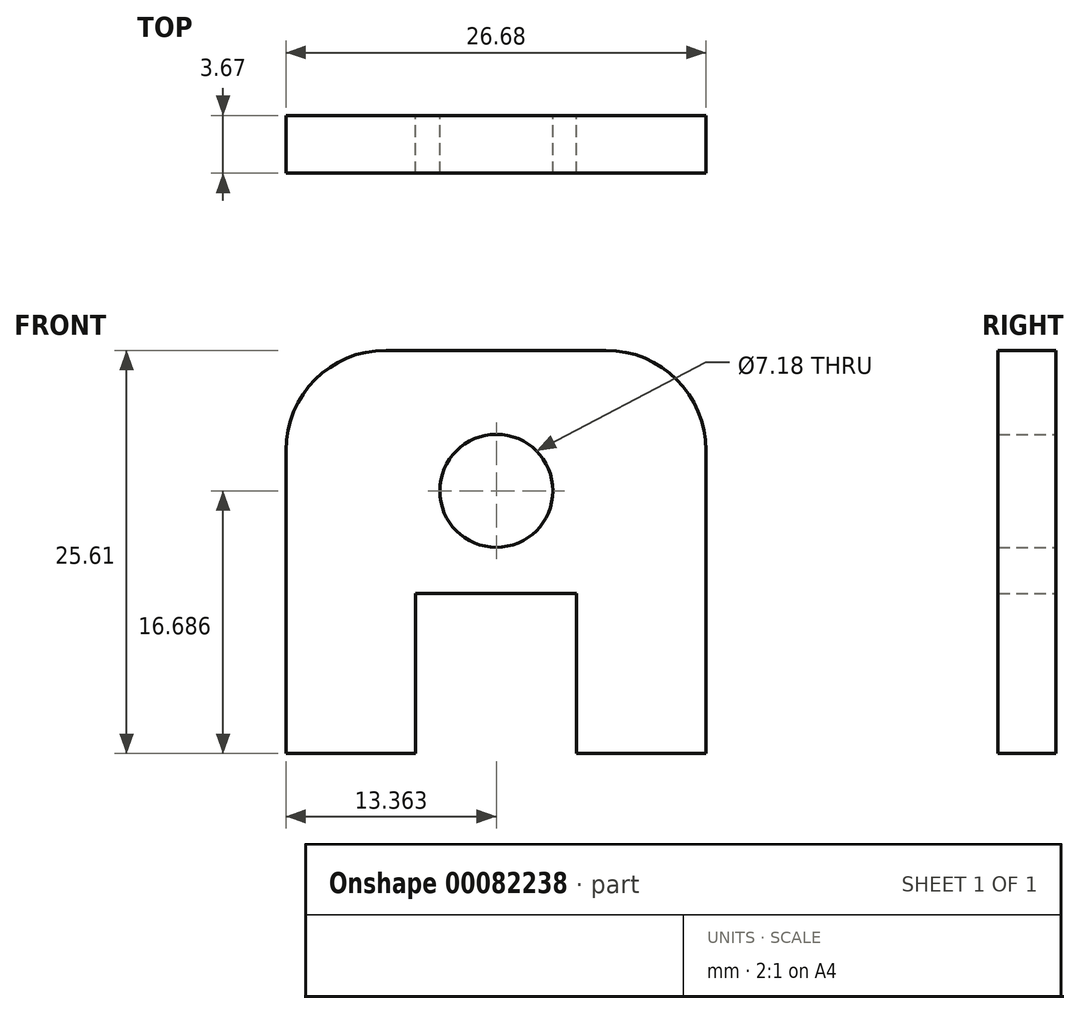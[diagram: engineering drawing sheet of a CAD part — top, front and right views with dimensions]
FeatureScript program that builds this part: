
annotation { "Feature Type Name" : "Feature", "Feature Type Description" : "" }
export const myFeature = defineFeature(function(context is Context, id is Id, definition is map)
    precondition{}
    {
        {
            var Q0;
            Q0=qCreatedBy(makeId("Front.planeOp"),FACE);
            var sketch = newSketch(context, id + "F0", { "sketchPlane" : qUnion([Q0])});
            skLineSegment(sketch, "E0", {"start": v(-46.74, 10.16) * mm, "end": v(-46.74, 0) * mm});
            skLineSegment(sketch, "E1", {"start": v(-46.74, 0) * mm, "end": v(-38.52, 0) * mm});
            skLineSegment(sketch, "E2", {"start": v(-38.52, 0) * mm, "end": v(-38.52, 10.16) * mm});
            skLineSegment(sketch, "E3", {"start": v(-38.52, 10.16) * mm, "end": v(-28.28, 10.16) * mm});
            skLineSegment(sketch, "E4", {"start": v(-28.28, 10.16) * mm, "end": v(-28.28, 0) * mm});
            skLineSegment(sketch, "E5", {"start": v(-28.28, 0) * mm, "end": v(-20.06, 0) * mm});
            skLineSegment(sketch, "E6", {"start": v(-20.06, 0) * mm, "end": v(-20.06, 10.16) * mm});
            skCircle(sketch, "E7", {"center": v(-33.38, 16.69) * mm, "radius": 3.59 * mm});
            skLineSegment(sketch, "E8", {"start": v(-46.74, 10.16) * mm, "end": v(-46.74, 19.26) * mm});
            skLineSegment(sketch, "E9", {"start": v(-20.06, 10.16) * mm, "end": v(-20.06, 19.26) * mm});
            skLineSegment(sketch, "E10", {"start": v(-40.4, 25.61) * mm, "end": v(-26.41, 25.61) * mm});
            skPoint(sketch, "E11.visualSharp", {"position": v(-46.74, 25.61) * mm});
            skArc(sketch, "E11.filletArc", {"start": v(-40.4, 25.61) * mm, "mid": v(-44.88, 23.75) * mm, "end": v(-46.74, 19.26) * mm});
            skPoint(sketch, "E12.visualSharp", {"position": v(-20.06, 25.61) * mm});
            skArc(sketch, "E12.filletArc", {"start": v(-20.06, 19.26) * mm, "mid": v(-21.92, 23.75) * mm, "end": v(-26.41, 25.61) * mm});
            skSolve(sketch);
        }
        {
            var Q0;
            Q0 = qSketchRegion(id + "F0", true);
            extrude(context, id + "F1", {"entities" : qUnion([Q0]), "depth" : 3.67 * mm});
        }
        {
            var Q0;
            Q0=makeQuery(id+"F1.opExtrude","CAP_FACE",FACE,{"disambiguationData":[OSD([sQuery(id+"F0.wireOp",EDGE,"E0"),sQuery(id+"F0.wireOp",EDGE,"E1"),sQuery(id+"F0.wireOp",EDGE,"E2"),sQuery(id+"F0.wireOp",EDGE,"E3"),sQuery(id+"F0.wireOp",EDGE,"E4"),sQuery(id+"F0.wireOp",EDGE,"E5"),sQuery(id+"F0.wireOp",EDGE,"E6"),sQuery(id+"F0.wireOp",EDGE,"G7WEZDjS-9yHr-iffs-nqtS-dOy6iPXBVwSC"),sQuery(id+"F0.wireOp",EDGE,"QYYBMkFr-ctql-qCKP-WJMF-hifE349vmNfA"),sQuery(id+"F0.wireOp",EDGE,"ODkR2BhN-TqlS-nnyb-9HyD-O0f0uBFYmDgr"),sQuery(id+"F0.wireOp",EDGE,"Adj53awA-v5Pa-xfxO-C1pp-XWefswGQPDUQ"),sQuery(id+"F0.wireOp",EDGE,"VbFsgx3R-cdNu-UVW6-uAL8-EwBlGGkYZxgK"),sQuery(id+"F0.wireOp",EDGE,"E7")])],"isStart":false});
            var sketch = newSketch(context, id + "F2", { "sketchPlane" : qUnion([Q0])});
            skLineSegment(sketch, "E13", {"start": v(-47.3, 28.35) * mm, "end": v(-4.5, 28.35) * mm});
            skLineSegment(sketch, "E14", {"start": v(-4.5, 28.35) * mm, "end": v(-4.5, 41.06) * mm});
            skLineSegment(sketch, "E15", {"start": v(-4.5, 41.06) * mm, "end": v(-53.65, 41.06) * mm});
            skLineSegment(sketch, "E16", {"start": v(-53.65, 41.06) * mm, "end": v(-53.65, 34.7) * mm});
            skPoint(sketch, "E17.visualSharp", {"position": v(-53.65, 28.35) * mm});
            skArc(sketch, "E17.filletArc", {"start": v(-53.65, 34.7) * mm, "mid": v(-51.8, 30.2) * mm, "end": v(-47.3, 28.35) * mm});
            skSolve(sketch);
        }
        {
            var Q0;
            Q0 = qSketchRegion(id + "F2", true);
            extrude(context, id + "F3", {"entities" : qUnion([Q0]), "operationType" : NewBodyOperationType.REMOVE, "endBound" : BoundingType.THROUGH_ALL, "oppositeDirection" : true, "depth" : 25.4 * mm});
        }
        {
            var Q0;
            Q0=makeQuery(id+"F1.opExtrude","CAP_FACE",FACE,{"disambiguationData":[OSD([sQuery(id+"F0.wireOp",EDGE,"E0"),sQuery(id+"F0.wireOp",EDGE,"E1"),sQuery(id+"F0.wireOp",EDGE,"E2"),sQuery(id+"F0.wireOp",EDGE,"E3"),sQuery(id+"F0.wireOp",EDGE,"E4"),sQuery(id+"F0.wireOp",EDGE,"E5"),sQuery(id+"F0.wireOp",EDGE,"E6"),sQuery(id+"F0.wireOp",EDGE,"G7WEZDjS-9yHr-iffs-nqtS-dOy6iPXBVwSC"),sQuery(id+"F0.wireOp",EDGE,"QYYBMkFr-ctql-qCKP-WJMF-hifE349vmNfA"),sQuery(id+"F0.wireOp",EDGE,"ODkR2BhN-TqlS-nnyb-9HyD-O0f0uBFYmDgr"),sQuery(id+"F0.wireOp",EDGE,"Adj53awA-v5Pa-xfxO-C1pp-XWefswGQPDUQ"),sQuery(id+"F0.wireOp",EDGE,"VbFsgx3R-cdNu-UVW6-uAL8-EwBlGGkYZxgK"),sQuery(id+"F0.wireOp",EDGE,"E7")])],"isStart":false});
            var sketch = newSketch(context, id + "F4", { "sketchPlane" : qUnion([Q0])});
            skLineSegment(sketch, "E18", {"start": v(-46.74, 0) * mm, "end": v(-46.74, 18.19) * mm});
            skLineSegment(sketch, "E19", {"start": v(-46.74, 18.19) * mm, "end": v(-53.65, 18.19) * mm});
            skLineSegment(sketch, "E20", {"start": v(-53.65, 18.19) * mm, "end": v(-53.65, 0) * mm});
            skLineSegment(sketch, "E21", {"start": v(-53.65, 0) * mm, "end": v(-46.74, 0) * mm});
            skLineSegment(sketch, "E22", {"start": v(-20.06, 0) * mm, "end": v(-20.06, 18.19) * mm});
            skLineSegment(sketch, "E23", {"start": v(-20.06, 18.19) * mm, "end": v(-13.16, 18.19) * mm});
            skLineSegment(sketch, "E24", {"start": v(-13.16, 18.19) * mm, "end": v(-13.16, 0) * mm});
            skLineSegment(sketch, "E25", {"start": v(-13.16, 0) * mm, "end": v(-20.06, 0) * mm});
            skSolve(sketch);
        }
        {
            var Q0;
            Q0 = qSketchRegion(id + "F4", true);
            extrude(context, id + "F5", {"entities" : qUnion([Q0]), "operationType" : NewBodyOperationType.REMOVE, "endBound" : BoundingType.THROUGH_ALL, "oppositeDirection" : true, "depth" : 25.4 * mm});
        }
    });
